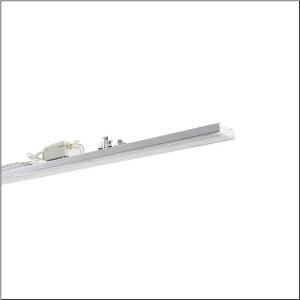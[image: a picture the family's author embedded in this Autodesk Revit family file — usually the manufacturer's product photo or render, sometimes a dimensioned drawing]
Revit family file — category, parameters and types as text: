
# Revit family: licross_11_recessed_ho_51te11dn4exs
name_source: partatom
category: Lighting Fixtures
units: mm (PartAtom-declared; Revit-internal decimal feet)

## family parameters
Cut with Voids When Loaded = No
Host = Face
Light Source = No
Part Type = Normal
Room Calculation Point = No
Round Connector Dimension = Use Diameter
Shared = No

## types (1)
- --- (1 x LED, 14000 lm, 76.8 W, 4000K)
    Apparent Load = 77 VA
    CIE Flux Codes = 87 95 99 100 100
    Color Rendering = 80
    Color Temperature = 4000K
    Default Elevation = 1800 mm
    Description = Licross 11 Recessed HO, luminaire insert, of sheet steel, galvanised, coil coated, white, length: 1.500mm, width: 66mm, height: 67mm, LED rated luminous flux: 14.000lm, light colour: 840, SDCM (Standard Deviation of Colour Matching)MacAdam ≤ 2 SDCM (initial), control gear: DALI 2, with plug, 5-pole, with phase selection, mains connection: 220..240V, AC, 50/60Hz, rated input power: 77W, internal wiring halogen-free, primary light control with lens, of plastic, primary optical cover: cover, of PMMA, light emission: direct distribution, primary light characteristic: symmetric, protection rating (complete): IP54, insulation class (complete): insulation class I (protective earthing), certification: CE, ENEC, VDE, UKCA, protection symbol: D if used in an environment with non-conductive dust loads with corresponding accessories, impact resistance: IK06, permissible ambient temperature for indoor applications: -25..+30°C, corresponds to IFS (International Featured Standards) requirements for safety and quality in the food industry, reducing of maximum allowable ambient temperature of 5°C with ceiling mounting, LABS conformity tested according to VDMA 24364:2018-05, The light source and the operating device comply with the requirements of the Ecodesign Regulation (EU) 2019/2020 and are replaceable in accordance with this regulation, packaging unit: 1 piece
    Height = 58 mm
    Lamp = 1 x LED
    Lamp Light Flux = 14000 lm
    Lamp Power = 76.8 W
    Lamp count = 1
    Length = 1500 mm
    Luminous efficacy = 182 lm/W
    Manufacturer = Siteco
    ModVariant = No
    Model = 51TE11DN4EXS
    Mounting Place = Ceiling
    Mounting Type = Pendant
    Number of Poles = 1
    OnlyDefault = Yes
    Power Factor = 1
    Product Name = Licross 11 Recessed HO
    Product group = luminaire insert | ceiling pendant
    ProductGroupID = 901
    Protection Class = Protection class I
    Protection Degree = IP 54
    RLX_Detail_Level = 1
    RLX_Emergency_Light_Flux = 0 lm
    RLX_Emergency_Type = 0
    RLX_Emergency_Type_DB = No
    RlxData = <blob elided: 24873 chars, md5=b1b94ce3>
    Socket = socket
    Standby Power = 0 W
    System Light Flux = 14000 lm
    System Power = 77 W
    Type Comments = factory setting: luminous flux: 100 % | dim-lin: 254 | 522 mA
    Type Image = l_1296930.jpg
    URL = http://relux.com
    VarID = @adj_102001
    Voltage = 0 V
    Weight = 0.00 kg
    Width = 66 mm

## geometry (parser evidence)
native form markers: Blend x4, Sweep x12
no freeform markers — native parametric forms only
